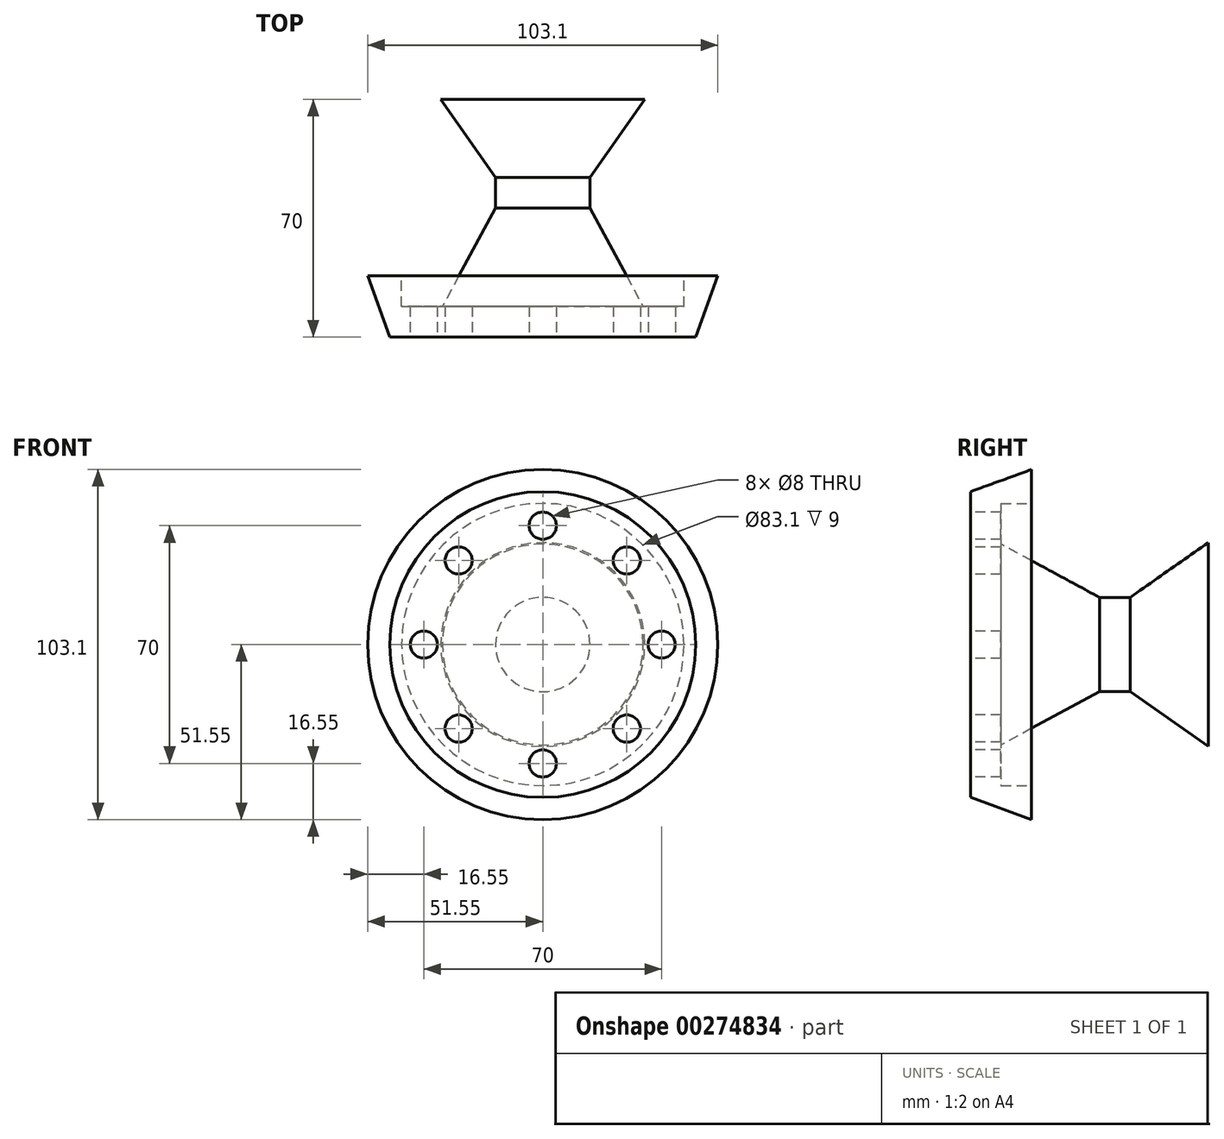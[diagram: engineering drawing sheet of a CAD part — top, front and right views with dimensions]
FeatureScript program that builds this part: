
annotation { "Feature Type Name" : "Feature", "Feature Type Description" : "" }
export const myFeature = defineFeature(function(context is Context, id is Id, definition is map)
    precondition{}
    {
        {
            var Q0;
            Q0=qCreatedBy(makeId("Top.planeOp"),FACE);
            var sketch = newSketch(context, id + "F0", { "sketchPlane" : qUnion([Q0])});
            skLineSegment(sketch, "E0", {"start": v(0, 0) * mm, "end": v(-45, 0) * mm});
            skLineSegment(sketch, "E1", {"start": v(-45, 0) * mm, "end": v(-51.55, 18) * mm});
            skLineSegment(sketch, "E2", {"start": v(-51.55, 18) * mm, "end": v(-41.55, 18) * mm});
            skLineSegment(sketch, "E3", {"start": v(-41.55, 18) * mm, "end": v(-41.55, 9) * mm});
            skLineSegment(sketch, "E4", {"start": v(-41.55, 9) * mm, "end": v(-29.55, 9) * mm});
            skLineSegment(sketch, "E5", {"start": v(-29.55, 9) * mm, "end": v(-13.9, 38) * mm});
            skLineSegment(sketch, "E6", {"start": v(-13.9, 38) * mm, "end": v(-13.9, 47) * mm});
            skLineSegment(sketch, "E7", {"start": v(-13.9, 47) * mm, "end": v(-30, 70) * mm});
            skLineSegment(sketch, "E8", {"start": v(-30, 70) * mm, "end": v(0, 70) * mm});
            skLineSegment(sketch, "E9", {"start": v(0, 70) * mm, "end": v(0, 0) * mm});
            skSolve(sketch);
        }
        {
            var Q0;
            Q0=makeQuery(id+"F0.imprint","IMPRINT",FACE,{"disambiguationData":[TD([[makeQuery(id+"F0.imprint","IMPRINT",EDGE,{"derivedFrom":sQuery(id+"F0.wireOp",EDGE,"E0")}),-1.0]])]});
            var Q1;
            Q1=sQuery(id+"F0.wireOp",EDGE,"E9");
            revolve(context, id + "F1", {"entities" : qUnion([Q0]), "axis" : qUnion([Q1]), "revolveType" : RevolveType.FULL});
        }
        {
            var Q0;
            Q0=qCreatedBy(makeId("Front.planeOp"),FACE);
            var sketch = newSketch(context, id + "F2", { "sketchPlane" : qUnion([Q0])});
            skCircle(sketch, "E10", {"center": v(0, 35) * mm, "radius": 4 * mm});
            skCircle(sketch, "E11.1.0", {"center": v(-24.75, 24.75) * mm, "radius": 4 * mm});
            skCircle(sketch, "E11.2.0", {"center": v(-35, 0) * mm, "radius": 4 * mm});
            skCircle(sketch, "E11.3.0", {"center": v(-24.75, -24.75) * mm, "radius": 4 * mm});
            skCircle(sketch, "E11.4.0", {"center": v(0, -35) * mm, "radius": 4 * mm});
            skCircle(sketch, "E11.5.0", {"center": v(24.75, -24.75) * mm, "radius": 4 * mm});
            skCircle(sketch, "E11.6.0", {"center": v(35, 0) * mm, "radius": 4 * mm});
            skCircle(sketch, "E11.7.0", {"center": v(24.75, 24.75) * mm, "radius": 4 * mm});
            skPoint(sketch, "E11.center", {"position": v(0, 0) * mm});
            skSolve(sketch);
        }
        {
            var Q0;
            Q0 = qSketchRegion(id + "F2", true);
            extrude(context, id + "F3", {"entities" : qUnion([Q0]), "operationType" : NewBodyOperationType.REMOVE, "oppositeDirection" : true, "depth" : 25 * mm});
        }
    });
